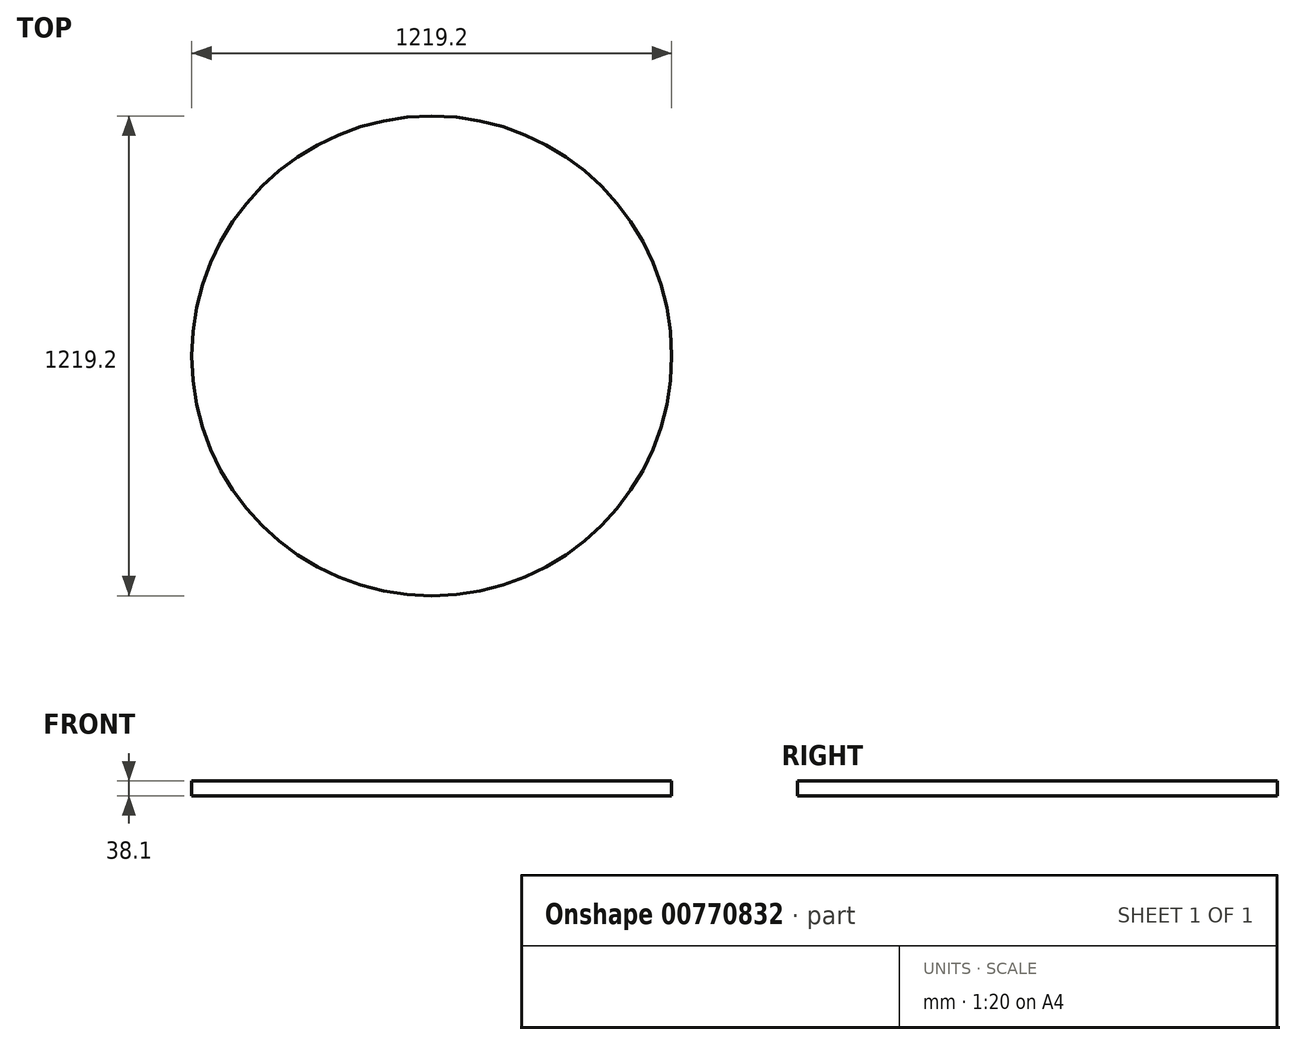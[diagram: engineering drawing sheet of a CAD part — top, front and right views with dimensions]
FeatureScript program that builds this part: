
annotation { "Feature Type Name" : "Feature", "Feature Type Description" : "" }
export const myFeature = defineFeature(function(context is Context, id is Id, definition is map)
    precondition{}
    {
        {
            var Q0;
            Q0=qCreatedBy(makeId("Top.planeOp"),FACE);
            var sketch = newSketch(context, id + "F0", { "sketchPlane" : qUnion([Q0])});
            skCircle(sketch, "E0", {"center": v(0, 0) * mm, "radius": 609.6 * mm});
            skSolve(sketch);
        }
        {
            var Q0;
            Q0 = qSketchRegion(id + "F0", true);
            extrude(context, id + "F1", {"entities" : qUnion([Q0]), "depth" : 38.1 * mm, "offsetDistance" : 25.4 * mm});
        }
    });
